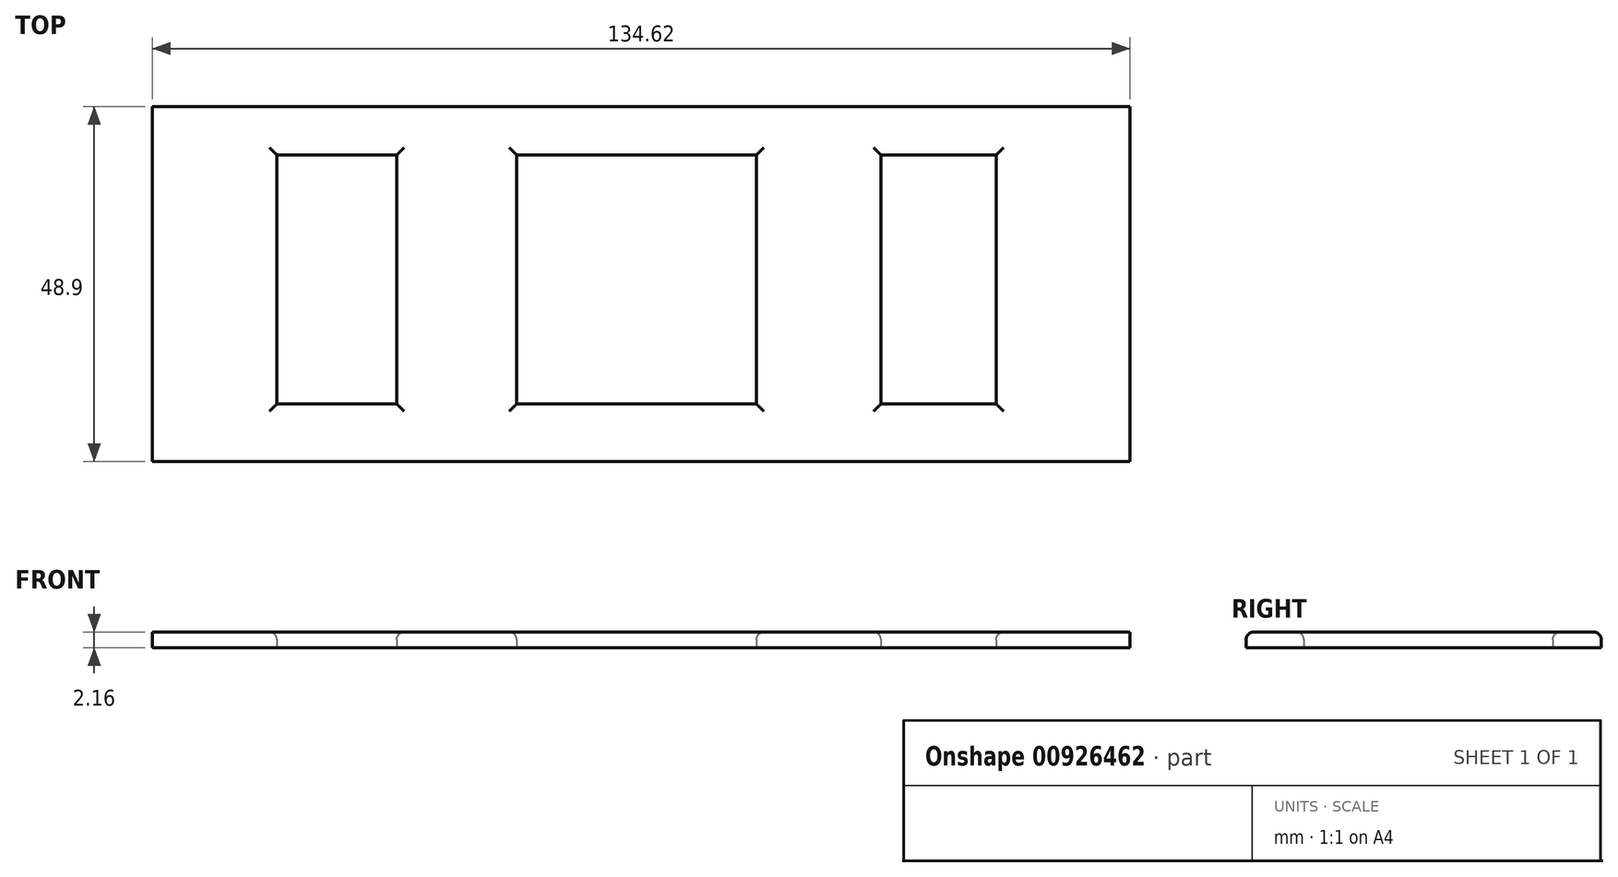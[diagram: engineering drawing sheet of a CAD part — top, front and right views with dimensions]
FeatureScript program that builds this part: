
annotation { "Feature Type Name" : "Feature", "Feature Type Description" : "" }
export const myFeature = defineFeature(function(context is Context, id is Id, definition is map)
    precondition{}
    {
        {
            var Q0;
            Q0=qCreatedBy(makeId("Top.planeOp"),FACE);
            var sketch = newSketch(context, id + "F0", { "sketchPlane" : qUnion([Q0])});
            skPoint(sketch, "E0.middle", {"position": v(0, 0) * mm});
            skLineSegment(sketch, "E1.bottom", {"start": v(-67.3, -24.45) * mm, "end": v(67.3, -24.45) * mm});
            skLineSegment(sketch, "E1.top", {"start": v(-67.3, 24.45) * mm, "end": v(67.3, 24.45) * mm});
            skLineSegment(sketch, "E1.left", {"start": v(-67.31, -24.45) * mm, "end": v(-67.3, 24.45) * mm});
            skLineSegment(sketch, "E1.right", {"start": v(67.31, -24.45) * mm, "end": v(67.31, 24.45) * mm});
            skLineSegment(sketch, "E2", {"start": v(33.02, 17.78) * mm, "end": v(33.02, -16.5) * mm});
            skLineSegment(sketch, "E3", {"start": v(67.31, 0) * mm, "end": v(67.31, 24.45) * mm});
            skLineSegment(sketch, "E4", {"start": v(67.31, 0) * mm, "end": v(67.31, -24.45) * mm});
            skLineSegment(sketch, "E5", {"start": v(-67.3, 24.45) * mm, "end": v(0, 24.45) * mm});
            skLineSegment(sketch, "E6", {"start": v(33.02, 24.45) * mm, "end": v(0, 24.45) * mm});
            skLineSegment(sketch, "E7", {"start": v(15.88, 17.78) * mm, "end": v(15.88, -16.5) * mm});
            skLineSegment(sketch, "E8", {"start": v(33.02, -24.45) * mm, "end": v(67.3, -24.45) * mm});
            skLineSegment(sketch, "E9", {"start": v(48.9, -16.5) * mm, "end": v(48.9, 17.78) * mm});
            skLineSegment(sketch, "E10", {"start": v(0, 24.45) * mm, "end": v(-67.3, 24.45) * mm});
            skLineSegment(sketch, "E11", {"start": v(-33.65, 17.78) * mm, "end": v(-33.65, -16.5) * mm});
            skLineSegment(sketch, "E12", {"start": v(-33.65, 24.45) * mm, "end": v(-67.3, 24.45) * mm});
            skLineSegment(sketch, "E13", {"start": v(-33.65, -24.45) * mm, "end": v(0, -24.45) * mm});
            skLineSegment(sketch, "E14", {"start": v(-17.14, -16.5) * mm, "end": v(-17.14, 17.78) * mm});
            skLineSegment(sketch, "E15", {"start": v(-67.31, 24.45) * mm, "end": v(-67.31, 10.48) * mm});
            skLineSegment(sketch, "E16", {"start": v(-50.16, 17.78) * mm, "end": v(-33.65, 17.78) * mm});
            skLineSegment(sketch, "E17", {"start": v(-67.31, -10.48) * mm, "end": v(-67.31, -24.45) * mm});
            skLineSegment(sketch, "E18", {"start": v(-50.16, -16.5) * mm, "end": v(-33.65, -16.5) * mm});
            skLineSegment(sketch, "E19.trimOffspring", {"start": v(-17.14, 17.78) * mm, "end": v(15.88, 17.78) * mm});
            skLineSegment(sketch, "E20.trimOffspring", {"start": v(-17.14, -16.5) * mm, "end": v(15.88, -16.5) * mm});
            skLineSegment(sketch, "E21.trimOffspring", {"start": v(33.02, 17.78) * mm, "end": v(48.9, 17.78) * mm});
            skLineSegment(sketch, "E22.trimOffspring", {"start": v(-50.16, 17.78) * mm, "end": v(-50.16, -16.5) * mm});
            skLineSegment(sketch, "E23.trimOffspring", {"start": v(33.02, -16.5) * mm, "end": v(48.9, -16.5) * mm});
            skSolve(sketch);
        }
        {
            var Q0;
            Q0 = qSketchRegion(id + "F0", true);
            extrude(context, id + "F1", {"entities" : qUnion([Q0]), "depth" : 2.16 * mm, "offsetDistance" : 25.4 * mm});
        }
        {
            var Q0;
            Q0=makeQuery(id+"F1.opExtrude","CAP_EDGE",EDGE,{"disambiguationData":[OSD([sQuery(id+"F0.wireOp",EDGE,"E7")])],"isStart":false});
            var Q1;
            Q1=makeQuery(id+"F1.opExtrude","CAP_EDGE",EDGE,{"disambiguationData":[OSD([sQuery(id+"F0.wireOp",EDGE,"E11")])],"isStart":false});
            var Q2;
            Q2=makeQuery(id+"F1.opExtrude","CAP_EDGE",EDGE,{"disambiguationData":[OSD([sQuery(id+"F0.wireOp",EDGE,"E14")])],"isStart":false});
            var Q3;
            Q3=makeQuery(id+"F1.opExtrude","CAP_EDGE",EDGE,{"disambiguationData":[OSD([sQuery(id+"F0.wireOp",EDGE,"E22.trimOffspring")])],"isStart":false});
            var Q4;
            Q4=makeQuery(id+"F1.opExtrude","CAP_EDGE",EDGE,{"disambiguationData":[OSD([sQuery(id+"F0.wireOp",EDGE,"E16")])],"isStart":false});
            var Q5;
            Q5=makeQuery(id+"F1.opExtrude","CAP_EDGE",EDGE,{"disambiguationData":[OSD([sQuery(id+"F0.wireOp",EDGE,"E19.trimOffspring")])],"isStart":false});
            var Q6;
            Q6=makeQuery(id+"F1.opExtrude","CAP_EDGE",EDGE,{"disambiguationData":[OSD([sQuery(id+"F0.wireOp",EDGE,"E20.trimOffspring")])],"isStart":false});
            var Q7;
            Q7=makeQuery(id+"F1.opExtrude","CAP_EDGE",EDGE,{"disambiguationData":[OSD([sQuery(id+"F0.wireOp",EDGE,"E18")])],"isStart":false});
            var Q8;
            Q8=makeQuery(id+"F1.opExtrude","CAP_EDGE",EDGE,{"disambiguationData":[OSD([sQuery(id+"F0.wireOp",EDGE,"E23.trimOffspring")])],"isStart":false});
            var Q9;
            Q9=makeQuery(id+"F1.opExtrude","CAP_EDGE",EDGE,{"disambiguationData":[OSD([sQuery(id+"F0.wireOp",EDGE,"E2")])],"isStart":false});
            var Q10;
            Q10=makeQuery(id+"F1.opExtrude","CAP_EDGE",EDGE,{"disambiguationData":[OSD([sQuery(id+"F0.wireOp",EDGE,"E21.trimOffspring")])],"isStart":false});
            var Q11;
            Q11=makeQuery(id+"F1.opExtrude","CAP_EDGE",EDGE,{"disambiguationData":[OSD([sQuery(id+"F0.wireOp",EDGE,"E9")])],"isStart":false});
            var Q12;
            Q12=makeQuery(id+"F1.opExtrude","CAP_EDGE",EDGE,{"disambiguationData":[OSD([sQuery(id+"F0.wireOp",EDGE,"E1.bottom"),sQuery(id+"F0.wireOp",EDGE,"E8"),sQuery(id+"F0.wireOp",EDGE,"E13")])],"isStart":false});
            var Q13;
            Q13=makeQuery(id+"F1.opExtrude","CAP_EDGE",EDGE,{"disambiguationData":[OSD([sQuery(id+"F0.wireOp",EDGE,"E1.top"),sQuery(id+"F0.wireOp",EDGE,"E6"),sQuery(id+"F0.wireOp",EDGE,"E10"),sQuery(id+"F0.wireOp",EDGE,"E12")])],"isStart":false});
            var Q14;
            Q14=makeQuery(id+"F1.opExtrude","CAP_EDGE",EDGE,{"disambiguationData":[OSD([sQuery(id+"F0.wireOp",EDGE,"E3"),sQuery(id+"F0.wireOp",EDGE,"E4")])],"isStart":false});
            fillet(context, id + "F2", {"entities" : qUnion([Q0, Q1, Q2, Q3, Q4, Q5, Q6, Q7, Q8, Q9, Q10, Q11, Q12, Q13, Q14]), "radius" : 1.02 * mm, "tangentPropagation" : true, "allowEdgeOverflow" : false});
        }
    });
